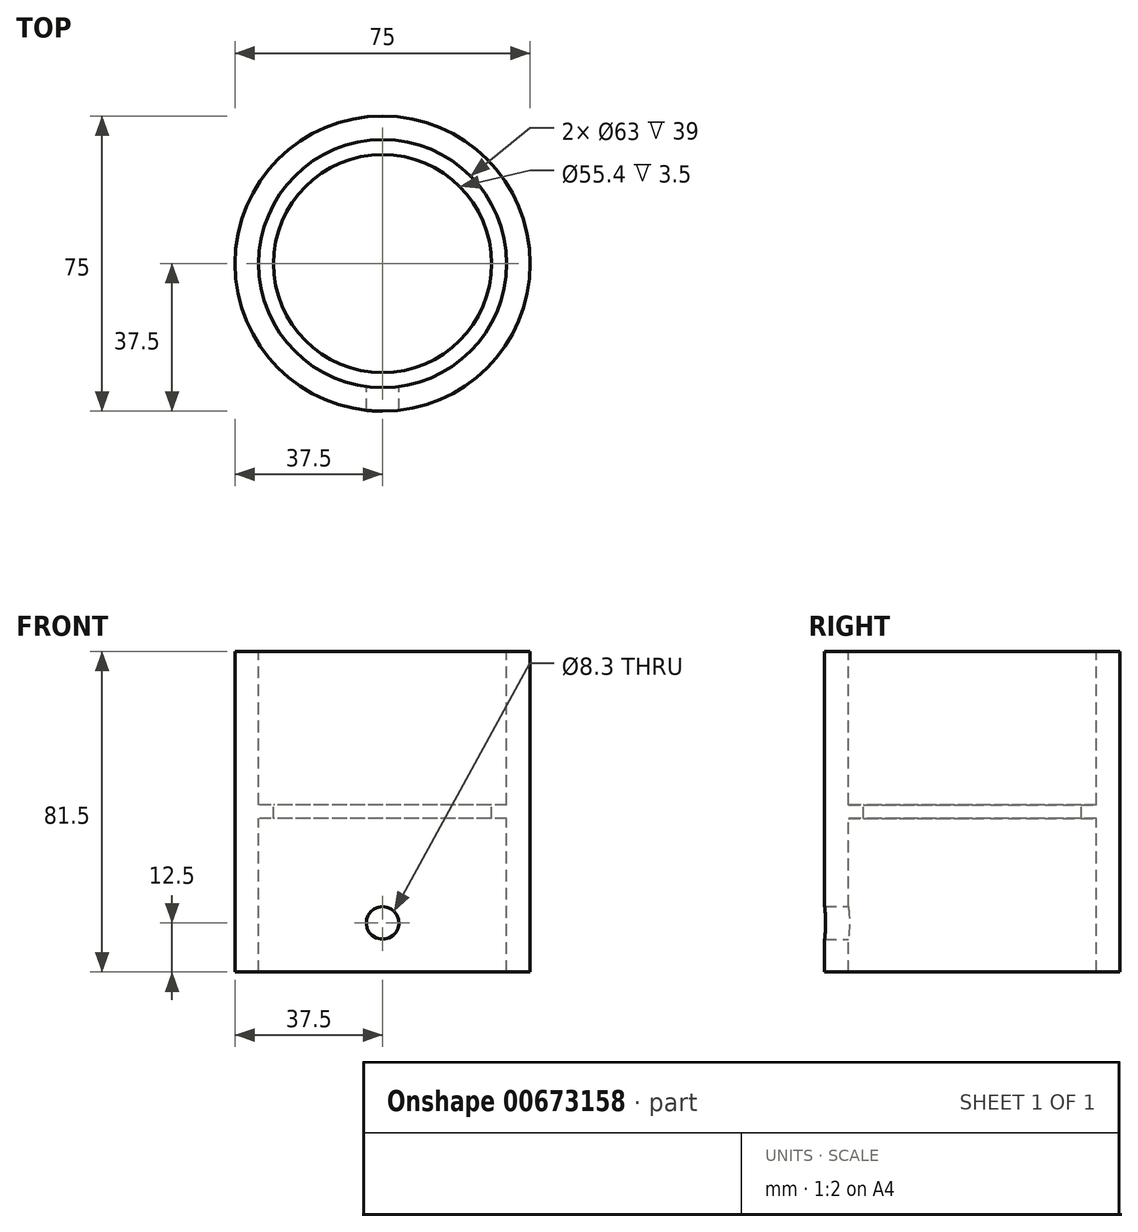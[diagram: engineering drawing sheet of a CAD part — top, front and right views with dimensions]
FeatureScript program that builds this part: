
annotation { "Feature Type Name" : "Feature", "Feature Type Description" : "" }
export const myFeature = defineFeature(function(context is Context, id is Id, definition is map)
    precondition{}
    {
        {
            var Q0;
            Q0=qCreatedBy(makeId("Front.planeOp"),FACE);
            var sketch = newSketch(context, id + "F0", { "sketchPlane" : qUnion([Q0])});
            skLineSegment(sketch, "E0", {"start": v(-37.5, 0) * mm, "end": v(-37.5, 81.5) * mm});
            skLineSegment(sketch, "E1", {"start": v(-37.5, 81.5) * mm, "end": v(-31.5, 81.5) * mm});
            skLineSegment(sketch, "E2", {"start": v(-31.5, 81.5) * mm, "end": v(-31.5, 42.5) * mm});
            skLineSegment(sketch, "E3", {"start": v(-31.5, 42.5) * mm, "end": v(-27.7, 42.5) * mm});
            skLineSegment(sketch, "E4", {"start": v(-27.7, 42.5) * mm, "end": v(-27.7, 39) * mm});
            skLineSegment(sketch, "E5", {"start": v(-27.7, 39) * mm, "end": v(-31.5, 39) * mm});
            skLineSegment(sketch, "E6", {"start": v(-31.5, 39) * mm, "end": v(-31.5, 0) * mm});
            skLineSegment(sketch, "E7", {"start": v(-31.5, 0) * mm, "end": v(-37.5, 0) * mm});
            skLineSegment(sketch, "E8", {"start": v(0, 0) * mm, "end": v(0, -22.63) * mm});
            skSolve(sketch);
        }
        {
            var Q0;
            Q0=makeQuery(id+"F0.imprint","IMPRINT",FACE,{"disambiguationData":[TD([[makeQuery(id+"F0.imprint","IMPRINT",EDGE,{"derivedFrom":sQuery(id+"F0.wireOp",EDGE,"E0")}),-1.0]])]});
            var Q1;
            Q1=sQuery(id+"F0.wireOp",EDGE,"E8");
            revolve(context, id + "F1", {"entities" : qUnion([Q0]), "axis" : qUnion([Q1]), "revolveType" : RevolveType.FULL});
        }
        {
            var Q0;
            Q0=qCreatedBy(makeId("Front.planeOp"),FACE);
            var sketch = newSketch(context, id + "F2", { "sketchPlane" : qUnion([Q0])});
            skCircle(sketch, "E9", {"center": v(0, 12.5) * mm, "radius": 4.15 * mm});
            skSolve(sketch);
        }
        {
            var Q0;
            Q0 = qSketchRegion(id + "F2", true);
            extrude(context, id + "F3", {"entities" : qUnion([Q0]), "operationType" : NewBodyOperationType.REMOVE, "depth" : 40 * mm, "offsetDistance" : 25 * mm});
        }
    });
